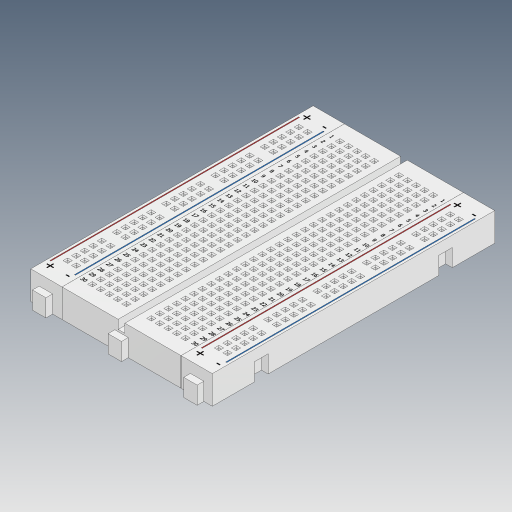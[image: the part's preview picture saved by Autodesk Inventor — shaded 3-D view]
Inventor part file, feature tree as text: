
AUTODESK INVENTOR PART (.ipt)
format: ipt  version: 2023.2 (Build 272271000, 271)  size: 5,271,552 bytes
history: native  units: mm
features: extrude x14, sketch x12, other x4, chamfer x2, pattern_linear x2, mirror x1
ambient origin geometry x8: Origin, YZ Plane, XZ Plane, XY Plane, X Axis, Y Axis, Z Axis, Center Point
bodies: Solido1 (feature_tree)
feature tree (35):
  extrude  "Estrusione1"  Depth=54.0mm
  extrude  "Estrusione2"  Depth=84.0mm
  extrude  "Estrusione3"  Depth=8.4mm TaperAngle=0.0deg
  extrude  "Estrusione4"  Depth=5.2mm
  extrude  "Estrusione5"  Depth=4.0mm
  extrude  "Estrusione6"  Depth=4.0mm
  extrude  "Estrusione7"  Depth=12.6mm
  sketch  "Schizzo11"
  extrude  "Estrusione8"  Depth=12.6mm
  extrude  "Estrusione9"  Depth=58.8mm
  sketch  "Schizzo12"
  extrude  "Estrusione10"  Depth=2.0mm TaperAngle=0.0deg
  extrude  "Estrusione11"  Depth=2.0mm TaperAngle=0.0deg
  extrude  "Estrusione12"  Depth=4.0mm
  chamfer  "Smusso1"  Distance=4.0mm
  pattern_linear  "Serie rettangolare1"  Spacing1=4.0mm  [1 undecoded]
  extrude  "Estrusione13"  Depth=2.5mm
  chamfer  "Smusso2"  Distance=2.5mm
  pattern_linear  "Serie rettangolare2"  Spacing1=2.0mm  [1 undecoded]
  other  "Piano di lavoro1"
  mirror  "Specchio1"
  extrude  "Estrusione14"  Depth=2.0mm TaperAngle=0.0deg
  sketch  "Schizzo4"
  sketch  "Schizzo5"
  sketch  "Schizzo6"
  sketch  "Schizzo7"
  sketch  "Schizzo8"
  other  "Linea chiusa proiettata1"
  other  "Linea chiusa proiettata2"
  other  "Linea chiusa proiettata3"
  sketch  "Schizzo9"
  sketch  "Schizzo10"
  sketch  "Schizzo13"
  sketch  "Schizzo14"
  sketch  "Schizzo15"
note: 2 required parameter values undecoded (feature->parameter linkage not recoverable at this tier; creation-order binding heuristic only, values carry confidence <= 0.55)
